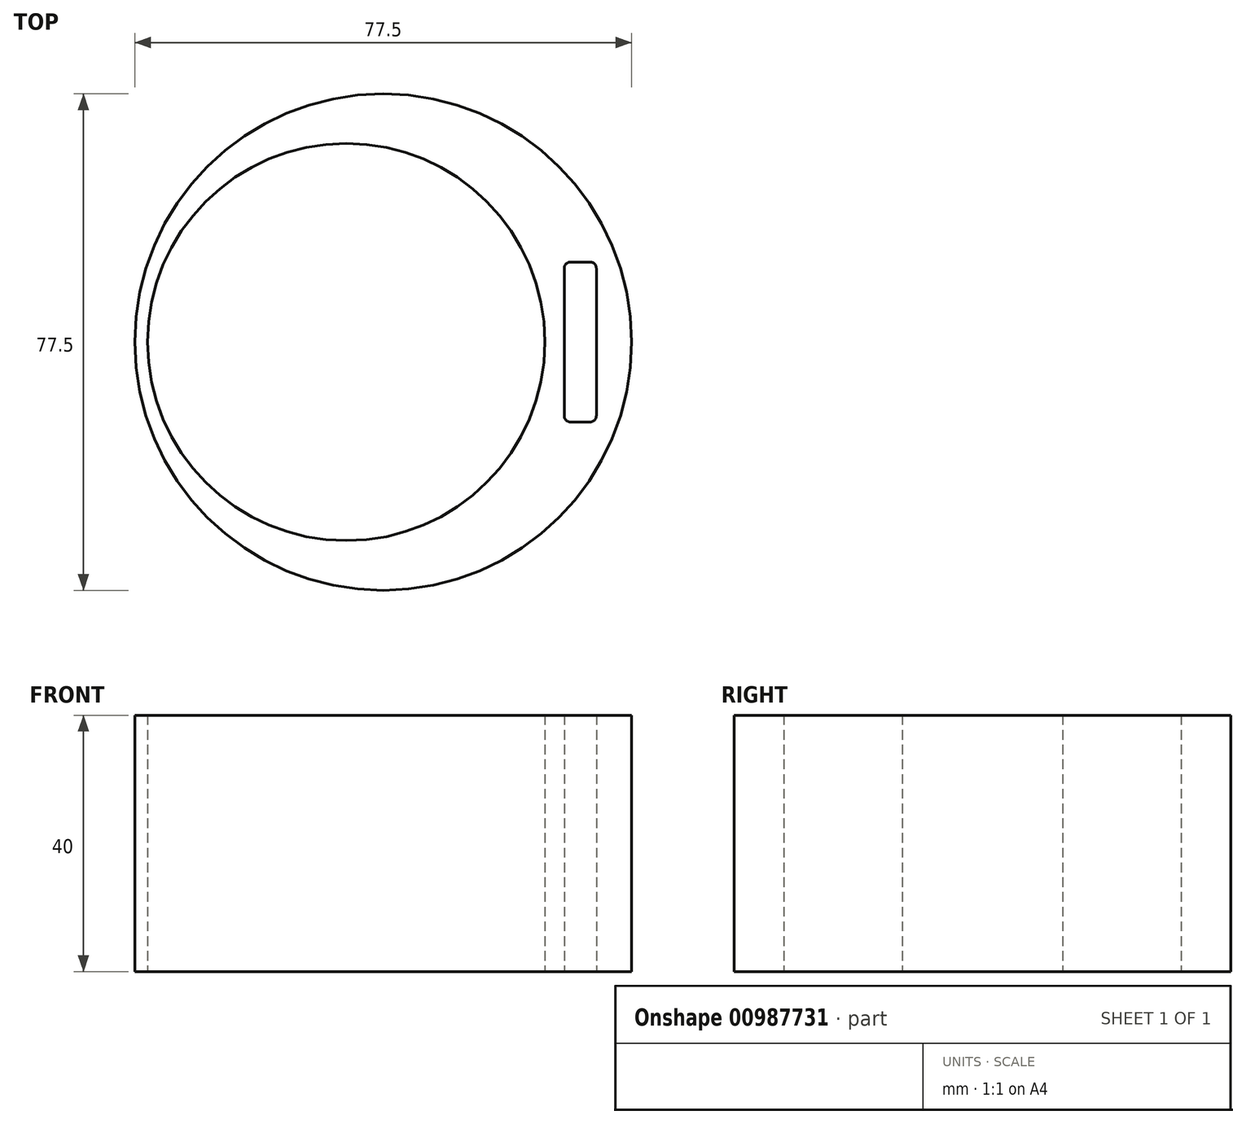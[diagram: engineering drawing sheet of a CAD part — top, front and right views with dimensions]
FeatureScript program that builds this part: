
annotation { "Feature Type Name" : "Feature", "Feature Type Description" : "" }
export const myFeature = defineFeature(function(context is Context, id is Id, definition is map)
    precondition{}
    {
        {
            var Q0;
            Q0=qCreatedBy(makeId("Top.planeOp"),FACE);
            var sketch = newSketch(context, id + "F0", { "sketchPlane" : qUnion([Q0])});
            skCircle(sketch, "E0", {"center": v(0, 0) * mm, "radius": 38.75 * mm});
            skCircle(sketch, "E1", {"center": v(-5.75, 0) * mm, "radius": 31 * mm});
            skLineSegment(sketch, "E2.bottom", {"start": v(32.26, -12.5) * mm, "end": v(29.26, -12.5) * mm});
            skLineSegment(sketch, "E2.top", {"start": v(32.26, 12.5) * mm, "end": v(29.26, 12.5) * mm});
            skLineSegment(sketch, "E2.left", {"start": v(33.26, -11.5) * mm, "end": v(33.26, 11.5) * mm});
            skLineSegment(sketch, "E2.right", {"start": v(28.26, -11.5) * mm, "end": v(28.26, 11.5) * mm});
            skPoint(sketch, "E2.middle", {"position": v(30.76, 0) * mm});
            skPoint(sketch, "E3.visualSharp", {"position": v(28.26, 12.5) * mm});
            skArc(sketch, "E3.filletArc", {"start": v(29.26, 12.5) * mm, "mid": v(28.55, 12.2) * mm, "end": v(28.26, 11.5) * mm});
            skPoint(sketch, "E4.visualSharp", {"position": v(33.26, 12.5) * mm});
            skArc(sketch, "E4.filletArc", {"start": v(33.26, 11.5) * mm, "mid": v(32.97, 12.2) * mm, "end": v(32.26, 12.5) * mm});
            skPoint(sketch, "E5.visualSharp", {"position": v(33.26, -12.5) * mm});
            skArc(sketch, "E5.filletArc", {"start": v(32.26, -12.5) * mm, "mid": v(32.97, -12.2) * mm, "end": v(33.26, -11.5) * mm});
            skPoint(sketch, "E6.visualSharp", {"position": v(28.26, -12.5) * mm});
            skArc(sketch, "E6.filletArc", {"start": v(28.26, -11.5) * mm, "mid": v(28.55, -12.2) * mm, "end": v(29.26, -12.5) * mm});
            skCircle(sketch, "E7", {"center": v(0, 0) * mm, "radius": 45.5 * mm});
            skSolve(sketch);
        }
        {
            var Q0;
            Q0=makeQuery(id+"F0.imprint","IMPRINT",FACE,{"disambiguationData":[TD([[makeQuery(id+"F0.imprint","IMPRINT",EDGE,{"derivedFrom":sQuery(id+"F0.wireOp",EDGE,"E0")}),1.0]])]});
            extrude(context, id + "F1", {"entities" : qUnion([Q0]), "depth" : 40 * mm, "offsetDistance" : 25 * mm});
        }
    });
